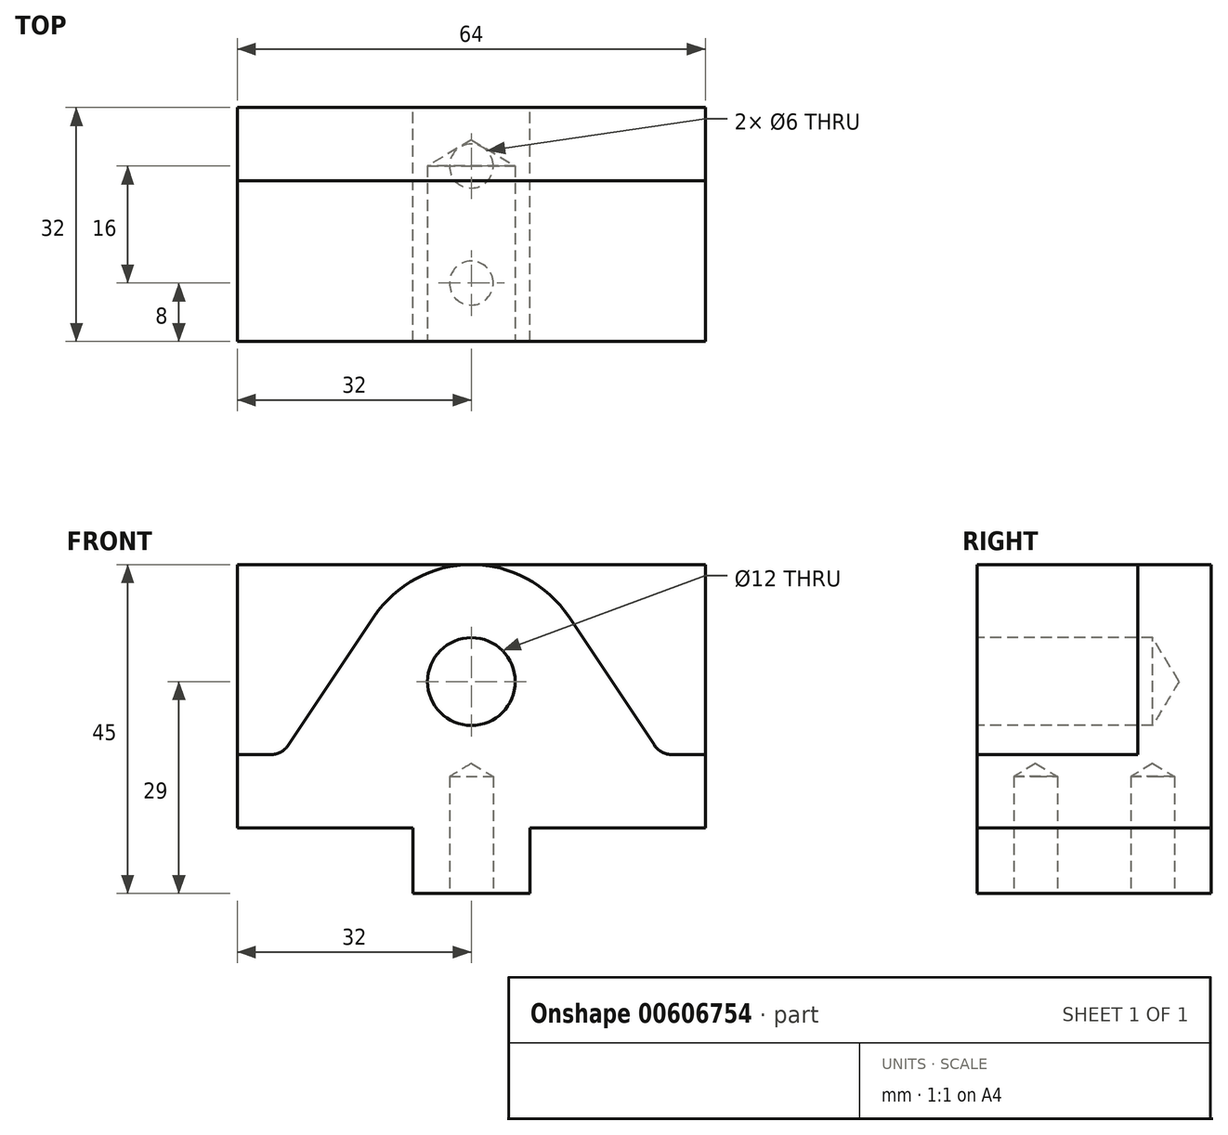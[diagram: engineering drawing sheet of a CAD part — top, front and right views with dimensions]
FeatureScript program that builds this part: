
annotation { "Feature Type Name" : "Feature", "Feature Type Description" : "" }
export const myFeature = defineFeature(function(context is Context, id is Id, definition is map)
    precondition{}
    {
        {
            var Q0;
            Q0=qCreatedBy(makeId("Front.planeOp"),FACE);
            var sketch = newSketch(context, id + "F0", { "sketchPlane" : qUnion([Q0])});
            skLineSegment(sketch, "E0.bottom", {"start": v(32, 18) * mm, "end": v(-32, 18) * mm});
            skLineSegment(sketch, "E0.top", {"start": v(32, -18) * mm, "end": v(8, -18) * mm});
            skLineSegment(sketch, "E0.left", {"start": v(32, 18) * mm, "end": v(32, -18) * mm});
            skLineSegment(sketch, "E0.right", {"start": v(-32, 18) * mm, "end": v(-32, -18) * mm});
            skPoint(sketch, "E0.middle", {"position": v(0, 0) * mm});
            skLineSegment(sketch, "E1.top", {"start": v(-8, -27) * mm, "end": v(8, -27) * mm});
            skLineSegment(sketch, "E1.left", {"start": v(-8, -18) * mm, "end": v(-8, -27) * mm});
            skLineSegment(sketch, "E1.right", {"start": v(8, -18) * mm, "end": v(8, -27) * mm});
            skLineSegment(sketch, "E2.trimOffspring", {"start": v(-8, -18) * mm, "end": v(-32, -18) * mm});
            skSolve(sketch);
        }
        {
            var Q0;
            Q0=makeQuery(id+"F0.imprint","IMPRINT",FACE,{"disambiguationData":[TD([[makeQuery(id+"F0.imprint","IMPRINT",EDGE,{"derivedFrom":sQuery(id+"F0.wireOp",EDGE,"E0.bottom")}),1.0]])]});
            extrude(context, id + "F1", {"entities" : qUnion([Q0]), "endBound" : BoundingType.SYMMETRIC, "depth" : 10 * mm, "offsetDistance" : 25.4 * mm});
        }
        {
            var Q0;
            Q0=makeQuery(id+"F1.opExtrude","CAP_FACE",FACE,{"disambiguationData":[OSD([sQuery(id+"F0.wireOp",EDGE,"E0.bottom"),sQuery(id+"F0.wireOp",EDGE,"E0.top"),sQuery(id+"F0.wireOp",EDGE,"E0.left"),sQuery(id+"F0.wireOp",EDGE,"E0.right"),sQuery(id+"F0.wireOp",EDGE,"E1.top"),sQuery(id+"F0.wireOp",EDGE,"E1.left"),sQuery(id+"F0.wireOp",EDGE,"E1.right"),sQuery(id+"F0.wireOp",EDGE,"E2.trimOffspring")])],"isStart":false});
            var sketch = newSketch(context, id + "F2", { "sketchPlane" : qUnion([Q0])});
            skLineSegment(sketch, "E3", {"start": v(-32, -8) * mm, "end": v(-27.5, -8) * mm});
            skLineSegment(sketch, "E4.MirrorCS", {"start": v(32, -8) * mm, "end": v(27.5, -8) * mm});
            skLineSegment(sketch, "E5.0", {"start": v(-32, -8) * mm, "end": v(-32, -18) * mm});
            skLineSegment(sketch, "E6.0", {"start": v(-8, -18) * mm, "end": v(-32, -18) * mm});
            skLineSegment(sketch, "E7.0", {"start": v(-8, -18) * mm, "end": v(-8, -27) * mm});
            skLineSegment(sketch, "E8.0", {"start": v(-8, -27) * mm, "end": v(8, -27) * mm});
            skLineSegment(sketch, "E9.0", {"start": v(8, -18) * mm, "end": v(8, -27) * mm});
            skLineSegment(sketch, "E10.0", {"start": v(32, -18) * mm, "end": v(8, -18) * mm});
            skLineSegment(sketch, "E11.0", {"start": v(32, -8) * mm, "end": v(32, -18) * mm});
            skPoint(sketch, "E12.orphan", {"position": v(-32, 18) * mm});
            skPoint(sketch, "E13.orphan", {"position": v(32, 18) * mm});
            skPoint(sketch, "E14.visualSharp", {"position": v(-27.5, -8) * mm});
            skArc(sketch, "E14.filletArc", {"start": v(-27.5, -8) * mm, "mid": v(-26.08, -7.64) * mm, "end": v(-25, -6.66) * mm});
            skPoint(sketch, "E15.visualSharp", {"position": v(27.5, -8) * mm});
            skArc(sketch, "E15.filletArc", {"start": v(25, -6.66) * mm, "mid": v(26.08, -7.64) * mm, "end": v(27.5, -8) * mm});
            skArc(sketch, "E16", {"start": v(13.31, 10.87) * mm, "mid": v(0, 18) * mm, "end": v(-13.31, 10.87) * mm});
            skLineSegment(sketch, "E17", {"start": v(-25, -6.66) * mm, "end": v(-13.31, 10.87) * mm});
            skLineSegment(sketch, "E18", {"start": v(13.31, 10.87) * mm, "end": v(25, -6.66) * mm});
            skSolve(sketch);
        }
        {
            var Q0;
            Q0=makeQuery(id+"F2.imprint","IMPRINT",FACE,{"disambiguationData":[TD([[makeQuery(id+"F2.imprint","IMPRINT",EDGE,{"derivedFrom":sQuery(id+"F2.wireOp",EDGE,"E3")}),-1.0]])]});
            extrude(context, id + "F3", {"entities" : qUnion([Q0]), "operationType" : NewBodyOperationType.ADD, "depth" : 22 * mm, "offsetDistance" : 25.4 * mm});
        }
        {
            var Q0;
            Q0=makeQuery(id+"F3.opExtrude","CAP_FACE",FACE,{"disambiguationData":[OSD([sQuery(id+"F2.wireOp",EDGE,"E3"),sQuery(id+"F2.wireOp",EDGE,"E4.MirrorCS"),sQuery(id+"F2.wireOp",EDGE,"E5.0"),sQuery(id+"F2.wireOp",EDGE,"E6.0"),sQuery(id+"F2.wireOp",EDGE,"E7.0"),sQuery(id+"F2.wireOp",EDGE,"E8.0"),sQuery(id+"F2.wireOp",EDGE,"E9.0"),sQuery(id+"F2.wireOp",EDGE,"E10.0"),sQuery(id+"F2.wireOp",EDGE,"E11.0"),sQuery(id+"F2.wireOp",EDGE,"E14.filletArc"),sQuery(id+"F2.wireOp",EDGE,"E15.filletArc"),sQuery(id+"F2.wireOp",EDGE,"E16"),sQuery(id+"F2.wireOp",EDGE,"E17"),sQuery(id+"F2.wireOp",EDGE,"E18")])],"isStart":false});
            var sketch = newSketch(context, id + "F4", { "sketchPlane" : qUnion([Q0])});
            skLineSegment(sketch, "E19.0.0", {"start": v(32, -18) * mm, "end": v(32, -8) * mm});
            skLineSegment(sketch, "E19.0.1", {"start": v(32, -8) * mm, "end": v(27.5, -8) * mm});
            skArc(sketch, "E19.0.2", {"start": v(27.5, -8) * mm, "mid": v(26.08, -7.64) * mm, "end": v(25, -6.66) * mm});
            skLineSegment(sketch, "E19.0.3", {"start": v(25, -6.66) * mm, "end": v(13.31, 10.87) * mm});
            skArc(sketch, "E19.0.4", {"start": v(13.31, 10.87) * mm, "mid": v(0, 18) * mm, "end": v(-13.31, 10.87) * mm});
            skLineSegment(sketch, "E19.0.5", {"start": v(-13.31, 10.87) * mm, "end": v(-25, -6.66) * mm});
            skArc(sketch, "E19.0.6", {"start": v(-25, -6.66) * mm, "mid": v(-26.08, -7.64) * mm, "end": v(-27.5, -8) * mm});
            skLineSegment(sketch, "E19.0.7", {"start": v(-27.5, -8) * mm, "end": v(-32, -8) * mm});
            skLineSegment(sketch, "E19.0.8", {"start": v(-32, -8) * mm, "end": v(-32, -18) * mm});
            skLineSegment(sketch, "E19.0.9", {"start": v(-32, -18) * mm, "end": v(-8, -18) * mm});
            skLineSegment(sketch, "E19.0.10", {"start": v(-8, -18) * mm, "end": v(-8, -27) * mm});
            skLineSegment(sketch, "E19.0.11", {"start": v(-8, -27) * mm, "end": v(8, -27) * mm});
            skLineSegment(sketch, "E19.0.12", {"start": v(8, -27) * mm, "end": v(8, -18) * mm});
            skLineSegment(sketch, "E19.0.13", {"start": v(8, -18) * mm, "end": v(32, -18) * mm});
            skSolve(sketch);
        }
        {
            var Q0;
            Q0=sQuery(id+"F4.wireOp",VERTEX,"E19.0.4.center");
            var Q1;
            Q1=makeQuery(id+"F1.opExtrude","SWEPT_BODY",BODY,{"disambiguationData":[OSD([sQuery(id+"F0.wireOp",EDGE,"E0.bottom"),sQuery(id+"F0.wireOp",EDGE,"E0.top"),sQuery(id+"F0.wireOp",EDGE,"E0.left"),sQuery(id+"F0.wireOp",EDGE,"E0.right"),sQuery(id+"F0.wireOp",EDGE,"E1.top"),sQuery(id+"F0.wireOp",EDGE,"E1.left"),sQuery(id+"F0.wireOp",EDGE,"E1.right"),sQuery(id+"F0.wireOp",EDGE,"E2.trimOffspring")])]});
            hole(context, id + "F5", {"style" : HoleStyle.SIMPLE, "endStyle" : HoleEndStyle.BLIND, "holeDiameter" : 12 * mm, "majorDiameter" : 6.35 * mm, "holeDepth" : 24 * mm, "isTappedThrough" : true, "tappedDepth" : 12.7 * mm, "tapClearance" : 3, "locations" : qUnion([Q0]), "scope" : qUnion([Q1])});
        }
        {
            var Q0;
            Q0=makeQuery(id+"F3.boolean.opBoolean","MERGE",FACE,{"derivedFrom":[makeQuery(id+"F1.opExtrude","SWEPT_FACE",FACE,{"disambiguationData":[OSD([sQuery(id+"F0.wireOp",EDGE,"E1.top")])]}),makeQuery(id+"F3.opExtrude","SWEPT_FACE",FACE,{"disambiguationData":[OSD([sQuery(id+"F2.wireOp",EDGE,"E8.0")])]})]});
            var sketch = newSketch(context, id + "F6", { "sketchPlane" : qUnion([Q0])});
            skPoint(sketch, "E20", {"position": v(0, 19) * mm});
            skPoint(sketch, "E21", {"position": v(0, 3) * mm});
            skSolve(sketch);
        }
        {
            var Q0;
            Q0=sQuery(id+"F6.wireOp",VERTEX,"E20");
            var Q1;
            Q1=sQuery(id+"F6.wireOp",VERTEX,"E21");
            var Q2;
            Q2=makeQuery(id+"F1.opExtrude","SWEPT_BODY",BODY,{"disambiguationData":[OSD([sQuery(id+"F0.wireOp",EDGE,"E0.bottom"),sQuery(id+"F0.wireOp",EDGE,"E0.top"),sQuery(id+"F0.wireOp",EDGE,"E0.left"),sQuery(id+"F0.wireOp",EDGE,"E0.right"),sQuery(id+"F0.wireOp",EDGE,"E1.top"),sQuery(id+"F0.wireOp",EDGE,"E1.left"),sQuery(id+"F0.wireOp",EDGE,"E1.right"),sQuery(id+"F0.wireOp",EDGE,"E2.trimOffspring")])]});
            hole(context, id + "F7", {"style" : HoleStyle.SIMPLE, "endStyle" : HoleEndStyle.BLIND, "holeDiameter" : 6 * mm, "majorDiameter" : 6.35 * mm, "holeDepth" : 16 * mm, "isTappedThrough" : true, "tappedDepth" : 12.7 * mm, "tapClearance" : 3, "startFromSketch" : true, "locations" : qUnion([Q0, Q1]), "scope" : qUnion([Q2])});
        }
    });
